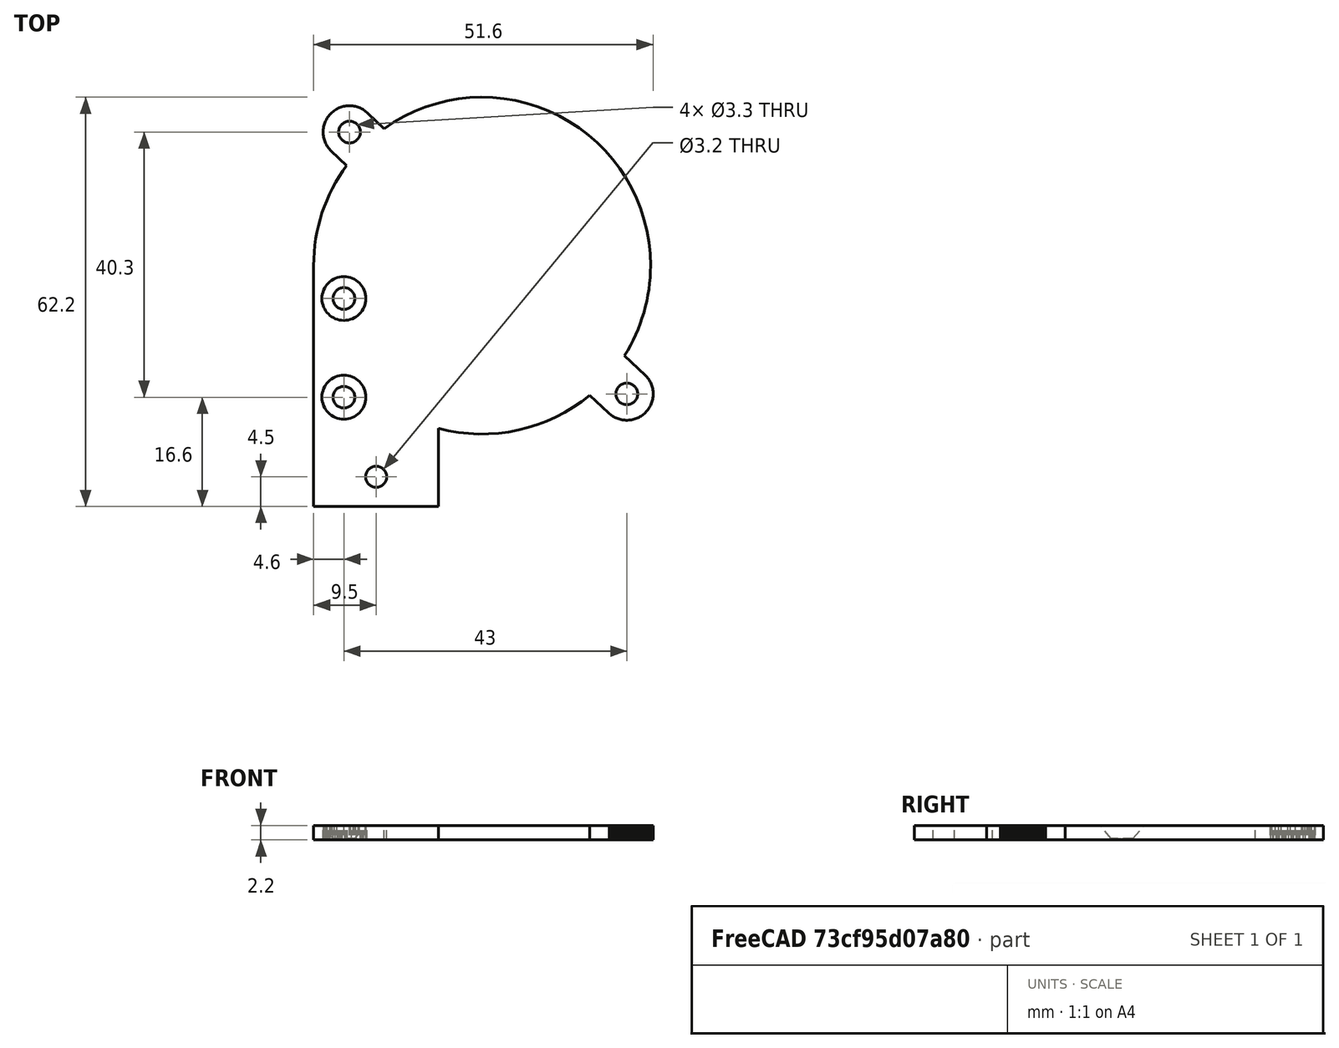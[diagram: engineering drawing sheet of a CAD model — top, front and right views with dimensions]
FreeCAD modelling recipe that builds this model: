
FCSTD DOCUMENT  (FreeCAD 0.19R)
Label: diamond-fan-holder
License: All rights reserved
LicenseURL: http://en.wikipedia.org/wiki/All_rights_reserved
objects: Part::Cylinder×8, Part::Fuse×6, Part::Box×2, Part::Cone×2, Part::FeaturePython×1, Part::Common×1, Part::MultiFuse×1, Part::Cut×1
note: 22 computed .brp shape members not serialized (recipe doc carries the construction recipe); baked Part::Feature solids carry a one-line shape summary decoded from their .brp

FEATURE [Part::Box] cube
  AttacherType = Attacher::AttachEngine3D
  Height = 2.2
  Length = 200
  Placement = pos=(-100,-100,0) rot=(0,0,1;0rad)
  Width = 200
FEATURE [Part::Box] cube001
  AttacherType = Attacher::AttachEngine3D
  Height = 15
  Length = 19
  Placement = pos=(0,-11,0) rot=(0,0,1;0rad)
  Width = 36.6
FEATURE [Part::Cylinder] cylinder
  Angle = 360
  AttacherType = Attacher::AttachEngine3D
  Height = 15
  Radius = 25.6
FEATURE [Part::Cylinder] cylinder001
  Angle = 360
  AttacherType = Attacher::AttachEngine3D
  Height = 15
  Placement = pos=(-20.15,20.3,0) rot=(0,0,1;0rad)
  Radius = 4
FEATURE [Part::Cylinder] cylinder002
  Angle = 360
  AttacherType = Attacher::AttachEngine3D
  Height = 15
  Placement = pos=(22,-19.5,0) rot=(0,0,1;0rad)
  Radius = 4
FEATURE [Part::FeaturePython] hull  # WARN: FeaturePython — macro-defined, semantics opaque (R4)
  Arguments = []
  Children = -> [cylinder001,cylinder002]
  Operation = hull
FEATURE [Part::Fuse] union
  Base = -> cylinder
  Placement = pos=(25.6,25.6,0) rot=(0,0,1;0rad)
  Tool = -> hull
FEATURE [Part::Fuse] union001
  Base = -> cube001
  Tool = -> union
FEATURE [Part::Common] intersection
  Base = -> cube
  Tool = -> union001
FEATURE [Part::Cylinder] cylinder003
  Angle = 360
  AttacherType = Attacher::AttachEngine3D
  Height = 10
  Placement = pos=(-20.15,20.3,-5) rot=(0,0,1;0rad)
  Radius = 1.65
FEATURE [Part::Cylinder] cylinder004
  Angle = 360
  AttacherType = Attacher::AttachEngine3D
  Height = 10
  Placement = pos=(22,-19.5,-5) rot=(0,0,1;0rad)
  Radius = 1.65
FEATURE [Part::Fuse] union002
  Base = -> cylinder003
  Placement = pos=(25.6,25.6,0) rot=(0,0,1;0rad)
  Tool = -> cylinder004
FEATURE [Part::Cylinder] cylinder005
  Angle = 360
  AttacherType = Attacher::AttachEngine3D
  Height = 10
  Placement = pos=(0,0,-5) rot=(0,0,1;0rad)
  Radius = 1.65
FEATURE [Part::Cone] cylinder006
  Angle = 360
  AttacherType = Attacher::AttachEngine3D
  Height = 2.2
  Placement = pos=(0,0,0.2) rot=(0,0,1;0rad)
  Radius1 = 1.65
  Radius2 = 3.5
FEATURE [Part::Fuse] union003
  Base = -> cylinder005
  Placement = pos=(-21,-5,0) rot=(0,0,1;0rad)
  Tool = -> cylinder006
FEATURE [Part::Cylinder] cylinder007
  Angle = 360
  AttacherType = Attacher::AttachEngine3D
  Height = 10
  Placement = pos=(0,0,-5) rot=(0,0,1;0rad)
  Radius = 1.65
FEATURE [Part::Cone] cylinder008
  Angle = 360
  AttacherType = Attacher::AttachEngine3D
  Height = 2.2
  Placement = pos=(0,0,0.2) rot=(0,0,1;0rad)
  Radius1 = 1.65
  Radius2 = 3.5
FEATURE [Part::Fuse] union004
  Base = -> cylinder007
  Placement = pos=(-21,-20,0) rot=(0,0,1;0rad)
  Tool = -> cylinder008
FEATURE [Part::Fuse] Group
  Base = -> union003
  Placement = pos=(25.6,25.6,0) rot=(0,0,1;0rad)
  Tool = -> union004
FEATURE [Part::Cylinder] cylinder009
  Angle = 360
  AttacherType = Attacher::AttachEngine3D
  Height = 10
  Placement = pos=(9.5,-6.5,-5) rot=(0,0,1;0rad)
  Radius = 1.6
FEATURE [Part::MultiFuse] union005
  Shapes = -> [union002,Group,cylinder009]
FEATURE [Part::Cut] difference
  Base = -> intersection
  Tool = -> union005
